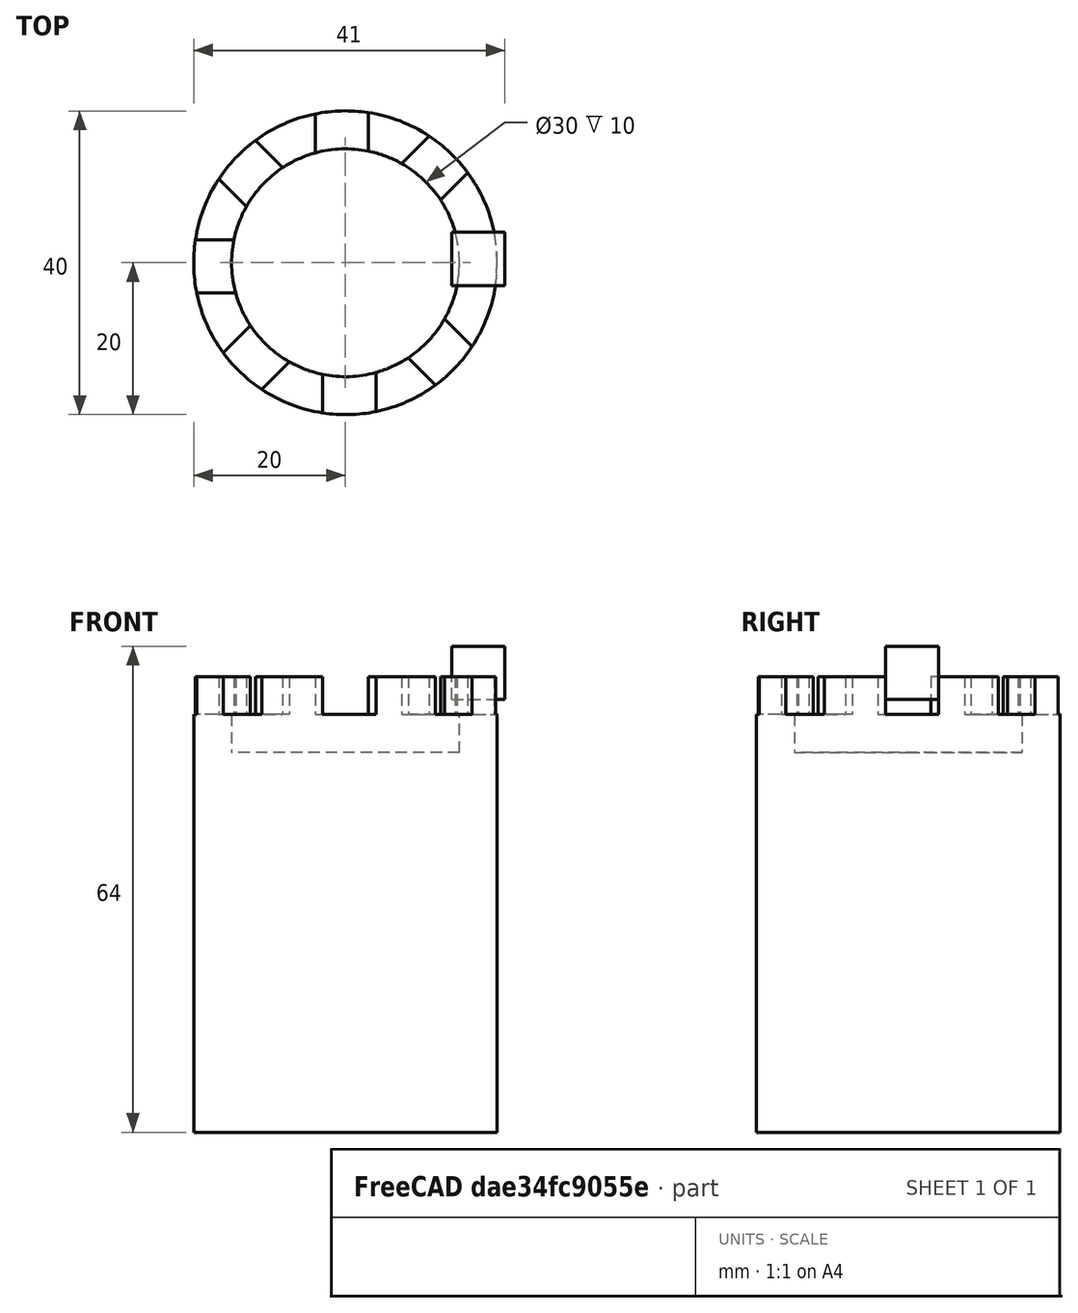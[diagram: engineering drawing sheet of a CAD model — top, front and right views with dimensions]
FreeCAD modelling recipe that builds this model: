
FCSTD DOCUMENT  (FreeCAD 1.0R39319 (Git))
Label: ojt1_t11r03_tower
License: All rights reserved
LicenseURL: https://en.wikipedia.org/wiki/All_rights_reserved
objects: Part::Cylinder×3, Part::Cut×2, Part::MultiFuse×1, Part::Box×1, Part::FeaturePython×1
note: 7 computed .brp shape members not serialized (recipe doc carries the construction recipe); baked Part::Feature solids carry a one-line shape summary decoded from their .brp

FEATURE [Part::Cylinder] Cylinder  label="Cilindre"
  Angle = 360
  AttacherType = Attacher::AttachEngine3D
  FirstAngle = 0
  Height = 50
  Radius = 20
  SecondAngle = 0
FEATURE [Part::Cylinder] Cylinder001  label="Cilindre001"
  Angle = 360
  AttacherType = Attacher::AttachEngine3D
  FirstAngle = 0
  Height = 20
  Placement = pos=(0,0,40) rot=(0,0,1;0rad)
  Radius = 20
  SecondAngle = 0
FEATURE [Part::Cylinder] Cylinder002  label="Cilindre002"
  Angle = 360
  AttacherType = Attacher::AttachEngine3D
  FirstAngle = 0
  Height = 10
  Placement = pos=(0,0,50) rot=(0,0,1;0rad)
  Radius = 15
  SecondAngle = 0
FEATURE [Part::Cut] Cut
  Base = -> Cylinder001
  Refine = true
  Tool = -> Cylinder002
FEATURE [Part::MultiFuse] Fusion
  Refine = true
  Shapes = -> [Cylinder,Cut]
FEATURE [Part::Box] Box  label="Cub"
  AttacherType = Attacher::AttachEngine3D
  Height = 7
  Length = 7
  Placement = pos=(14,-3,57) rot=(0,0,1;0rad)
  Width = 7
FEATURE [Part::FeaturePython] Array  # Draft array (typed FeaturePython)
  AlwaysSyncPlacement = false
  Angle = 360
  ArrayType = 1
  Axis = (0,0,1)
  Base = -> Box
  Center = (0,0,0)
  Count = 8
  ExpandArray = false
  Fuse = false
  IntervalAxis = (0,0,0)
  IntervalX = (50,0,0)
  IntervalY = (0,50,0)
  IntervalZ = (0,0,50)
  NumberCircles = 3
  NumberPolar = 8
  NumberX = 2
  NumberY = 2
  NumberZ = 1
  Placement = pos=(0,0,-2) rot=(0,0,1;0rad)
  PlacementList = 8 placements: [(14,-3,57),(12.0208,7.77817,57),(3,14,57),(-7.77817,12.0208,57),(-14,3,57),(-12.0208,-7.77817,57),(-3,-14,57),(7.77817,-12.0208,57)]
  RadialDistance = 50
  ScaleList = (8) [(1,1,1),(1,1,1),(1,1,1),(1,1,1),(1,1,1),(1,1,1),(1,1,1),(1,1,1)]
  Symmetry = 1
  TangentialDistance = 25
FEATURE [Part::Cut] Cut001
  Base = -> Fusion
  Refine = true
  Tool = -> Array
